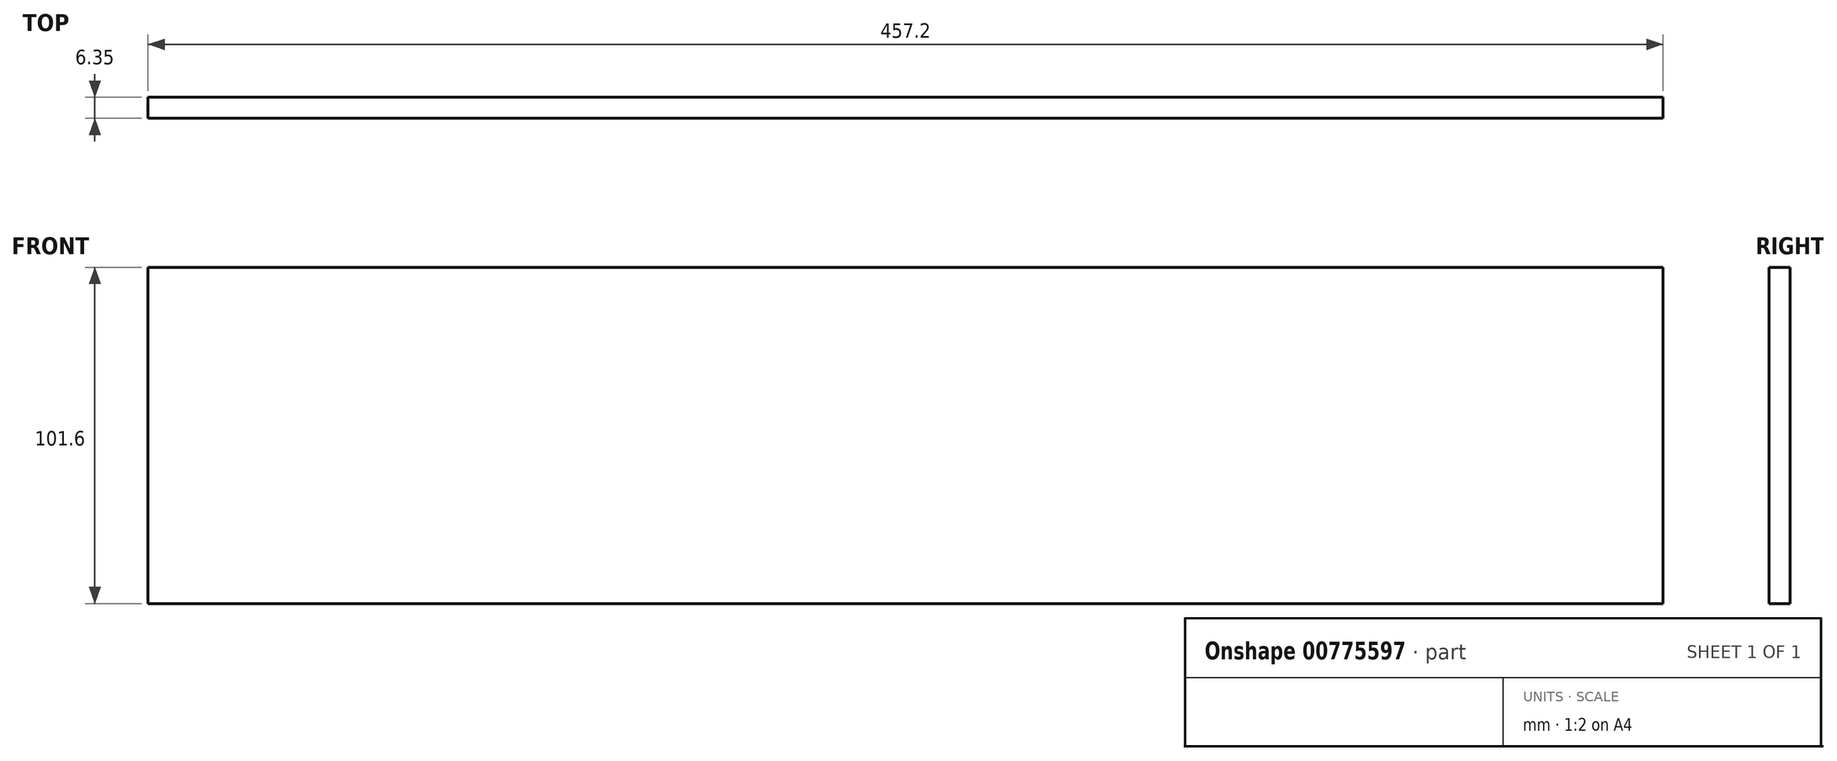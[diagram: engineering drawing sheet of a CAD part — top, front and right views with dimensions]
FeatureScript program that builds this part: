
annotation { "Feature Type Name" : "Feature", "Feature Type Description" : "" }
export const myFeature = defineFeature(function(context is Context, id is Id, definition is map)
    precondition{}
    {
        {
            var Q0;
            Q0=qCreatedBy(makeId("Front.planeOp"),FACE);
            var sketch = newSketch(context, id + "F0", { "sketchPlane" : qUnion([Q0])});
            skLineSegment(sketch, "E0.bottom", {"start": v(228.6, -50.8) * mm, "end": v(-228.6, -50.8) * mm});
            skLineSegment(sketch, "E0.top", {"start": v(228.6, 50.8) * mm, "end": v(-228.6, 50.8) * mm});
            skLineSegment(sketch, "E0.left", {"start": v(228.6, -50.8) * mm, "end": v(228.6, 50.8) * mm});
            skLineSegment(sketch, "E0.right", {"start": v(-228.6, -50.8) * mm, "end": v(-228.6, 50.8) * mm});
            skPoint(sketch, "E0.middle", {"position": v(0, 0) * mm});
            skSolve(sketch);
        }
        {
            var Q0;
            Q0 = qSketchRegion(id + "F0", true);
            extrude(context, id + "F1", {"entities" : qUnion([Q0]), "depth" : 6.35 * mm, "offsetDistance" : 25.4 * mm});
        }
    });
